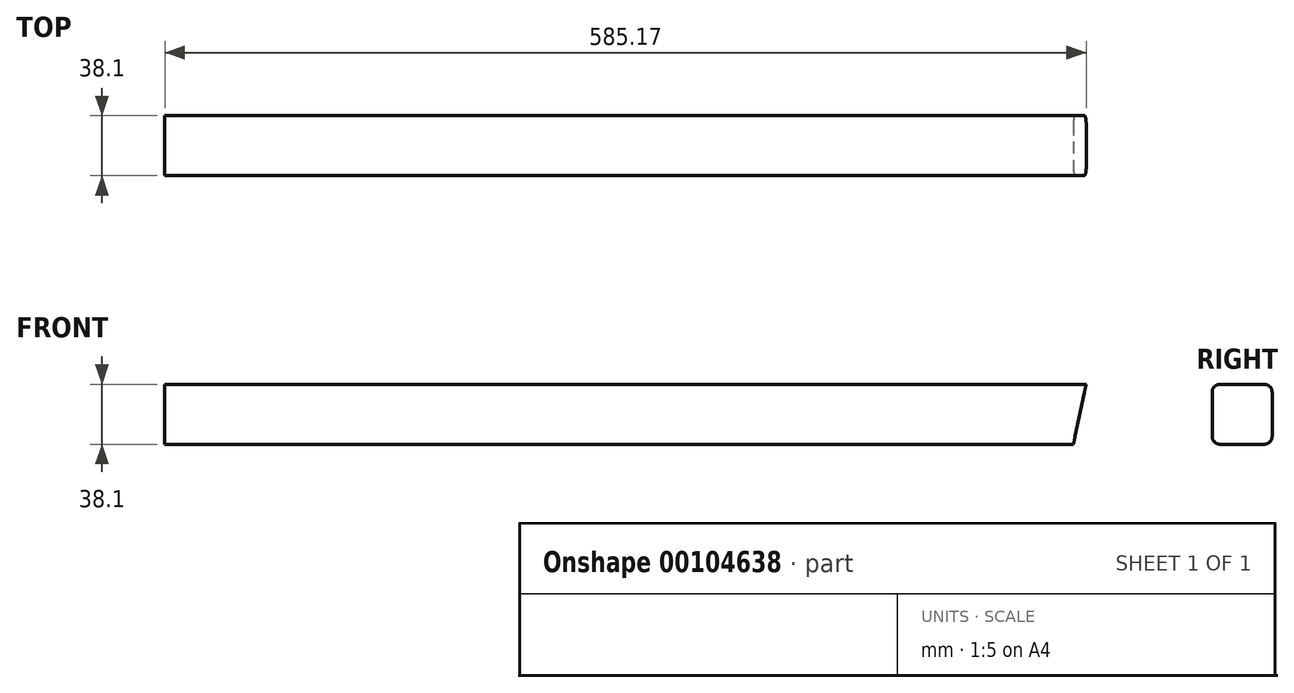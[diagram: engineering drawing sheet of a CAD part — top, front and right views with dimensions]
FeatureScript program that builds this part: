
annotation { "Feature Type Name" : "Feature", "Feature Type Description" : "" }
export const myFeature = defineFeature(function(context is Context, id is Id, definition is map)
    precondition{}
    {
        {
            var Q0;
            Q0=qCreatedBy(makeId("Front.planeOp"),FACE);
            var sketch = newSketch(context, id + "F0", { "sketchPlane" : qUnion([Q0])});
            skLineSegment(sketch, "E0.bottom", {"start": v(313.94, -19.05) * mm, "end": v(-313.94, -19.05) * mm});
            skLineSegment(sketch, "E0.top", {"start": v(313.94, 19.05) * mm, "end": v(-313.94, 19.05) * mm});
            skLineSegment(sketch, "E0.left", {"start": v(313.94, -19.05) * mm, "end": v(313.94, 19.05) * mm});
            skLineSegment(sketch, "E0.right", {"start": v(-313.94, -19.05) * mm, "end": v(-313.94, 19.05) * mm});
            skPoint(sketch, "E0.middle", {"position": v(0, 0) * mm});
            skSolve(sketch);
        }
        {
            var Q0;
            Q0=qSketchRegion(id+"F0",true);
            extrude(context, id + "F1", {"entities" : qUnion([Q0]), "endBound" : BoundingType.SYMMETRIC, "depth" : 38.1 * mm});
        }
        {
            var Q0;
            Q0=makeQuery(id+"F1.opExtrude","CAP_FACE",FACE,{"disambiguationData":[OSD([sQuery(id+"F0.wireOp",EDGE,"E0.bottom"),sQuery(id+"F0.wireOp",EDGE,"E0.top"),sQuery(id+"F0.wireOp",EDGE,"E0.left"),sQuery(id+"F0.wireOp",EDGE,"E0.right")])],"isStart":false});
            var sketch = newSketch(context, id + "F2", { "sketchPlane" : qUnion([Q0])});
            skLineSegment(sketch, "E1", {"start": v(271.23, 19.05) * mm, "end": v(263.13, -19.05) * mm});
            skLineSegment(sketch, "E2", {"start": v(263.13, -19.05) * mm, "end": v(313.94, -19.05) * mm});
            skLineSegment(sketch, "E3", {"start": v(313.94, -19.05) * mm, "end": v(313.94, 19.05) * mm});
            skLineSegment(sketch, "E4", {"start": v(313.94, 19.05) * mm, "end": v(271.23, 19.05) * mm});
            skLineSegment(sketch, "E5", {"start": v(267.18, 0) * mm, "end": v(313.94, 0) * mm, "construction": true});
            skSolve(sketch);
        }
        {
            var Q0;
            Q0=qSketchRegion(id+"F2",true);
            extrude(context, id + "F3", {"entities" : qUnion([Q0]), "operationType" : NewBodyOperationType.REMOVE, "endBound" : BoundingType.THROUGH_ALL, "oppositeDirection" : true, "depth" : 25.4 * mm});
        }
        {
            var Q0;
            Q0=makeQuery(id+"F1.opExtrude","CAP_EDGE",EDGE,{"disambiguationData":[OSD([sQuery(id+"F0.wireOp",EDGE,"E0.top")])],"isStart":false});
            var Q1;
            Q1=makeQuery(id+"F1.opExtrude","CAP_EDGE",EDGE,{"disambiguationData":[OSD([sQuery(id+"F0.wireOp",EDGE,"E0.bottom")])],"isStart":false});
            var Q2;
            Q2=makeQuery(id+"F1.opExtrude","CAP_EDGE",EDGE,{"disambiguationData":[OSD([sQuery(id+"F0.wireOp",EDGE,"E0.top")])],"isStart":true});
            var Q3;
            Q3=makeQuery(id+"F1.opExtrude","CAP_EDGE",EDGE,{"disambiguationData":[OSD([sQuery(id+"F0.wireOp",EDGE,"E0.bottom")])],"isStart":true});
            fillet(context, id + "F4", {"entities" : qUnion([Q0, Q1, Q2, Q3]), "radius" : 5.08 * mm, "tangentPropagation" : true, "allowEdgeOverflow" : false});
        }
    });
